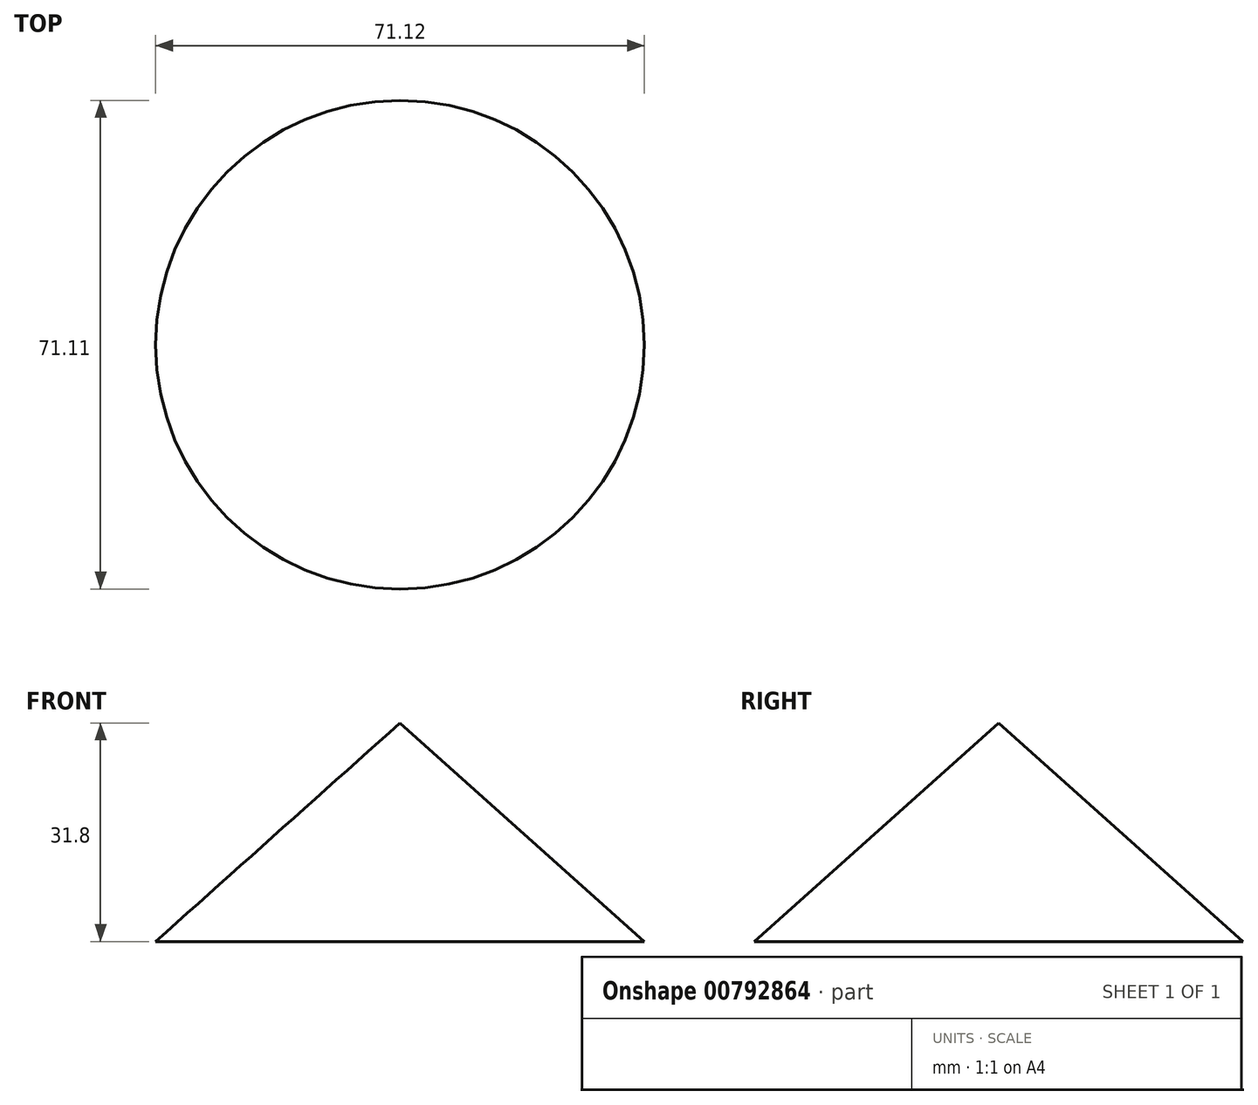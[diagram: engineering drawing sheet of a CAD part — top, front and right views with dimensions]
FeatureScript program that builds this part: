
annotation { "Feature Type Name" : "Feature", "Feature Type Description" : "" }
export const myFeature = defineFeature(function(context is Context, id is Id, definition is map)
    precondition{}
    {
        {
            var Q0;
            Q0=qCreatedBy(makeId("Right.planeOp"),FACE);
            var sketch = newSketch(context, id + "F0", { "sketchPlane" : qUnion([Q0])});
            skLineSegment(sketch, "E0", {"start": v(-35.56, 31.8) * mm, "end": v(-35.56, 0) * mm});
            skLineSegment(sketch, "E1", {"start": v(-35.56, 0) * mm, "end": v(0, 0) * mm});
            skLineSegment(sketch, "E2", {"start": v(0, 0) * mm, "end": v(-35.56, 31.8) * mm});
            skSolve(sketch);
        }
        {
            var Q0;
            Q0=makeQuery(id+"F0.imprint","IMPRINT",FACE,{"disambiguationData":[TD([[makeQuery(id+"F0.imprint","IMPRINT",EDGE,{"derivedFrom":sQuery(id+"F0.wireOp",EDGE,"E0")}),1.0]])]});
            var Q1;
            Q1=sQuery(id+"F0.wireOp",EDGE,"E2");
            var Q2;
            Q2=sQuery(id+"F0.wireOp",EDGE,"E1");
            var Q3;
            Q3=sQuery(id+"F0.wireOp",EDGE,"E0");
            var Q4;
            Q4=sQuery(id+"F0.wireOp",EDGE,"E0");
            revolve(context, id + "F1", {"surfaceOperationType" : NewSurfaceOperationType.NEW, "entities" : qUnion([Q0]), "surfaceEntities" : qUnion([Q1, Q2, Q3]), "axis" : qUnion([Q4]), "revolveType" : RevolveType.FULL});
        }
        {
            var Q0;
            Q0=qCreatedBy(makeId("Front.planeOp"),FACE);
            var sketch = newSketch(context, id + "F2", { "sketchPlane" : qUnion([Q0])});
            skLineSegment(sketch, "E3", {"start": v(-27.4, 18) * mm, "end": v(30.92, 18) * mm});
            skSolve(sketch);
        }
        {
            var Q0;
            Q0=sQuery(id+"F2.wireOp",EDGE,"E3");
            extrude(context, id + "F3", {"bodyType" : ToolBodyType.SURFACE, "surfaceEntities" : qUnion([Q0]), "depth" : 275.34 * mm, "offsetDistance" : 25.4 * mm, "symmetric" : true});
        }
    });
